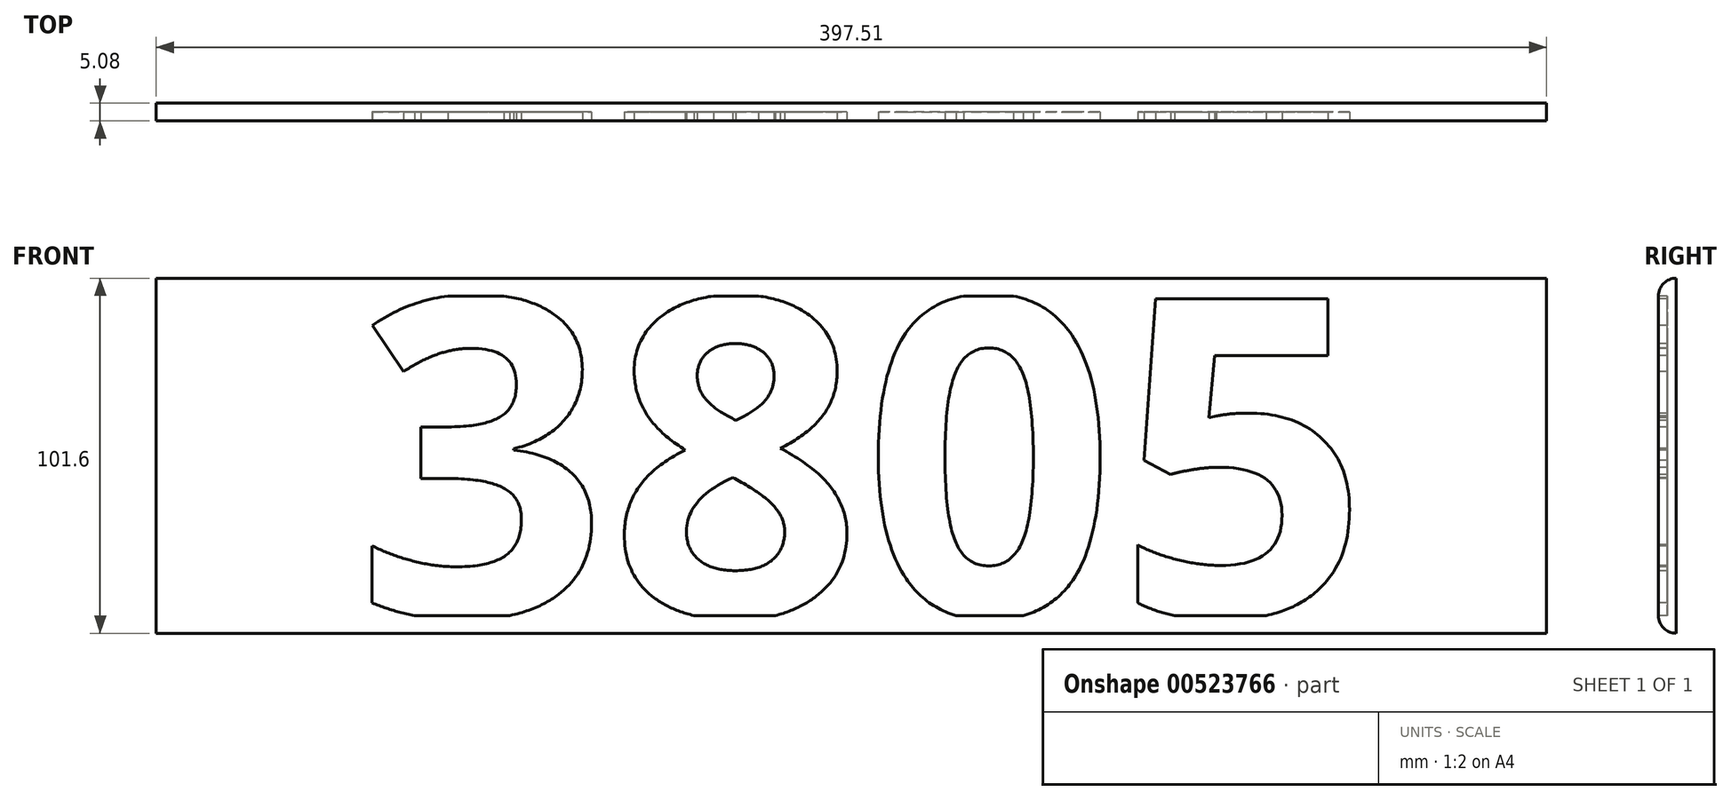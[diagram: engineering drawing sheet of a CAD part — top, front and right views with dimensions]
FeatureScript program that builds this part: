
annotation { "Feature Type Name" : "Feature", "Feature Type Description" : "" }
export const myFeature = defineFeature(function(context is Context, id is Id, definition is map)
    precondition{}
    {
        {
            var Q0;
            Q0=qCreatedBy(makeId("Right.planeOp"),FACE);
            var sketch = newSketch(context, id + "F0", { "sketchPlane" : qUnion([Q0])});
            skLineSegment(sketch, "E0", {"start": v(0, 0) * mm, "end": v(0, 101.6) * mm});
            skLineSegment(sketch, "E1", {"start": v(0, 101.6) * mm, "end": v(0, 101.6) * mm});
            skLineSegment(sketch, "E2", {"start": v(-5.08, 96.52) * mm, "end": v(-5.08, 5.08) * mm});
            skLineSegment(sketch, "E3", {"start": v(0, 0) * mm, "end": v(0, 0) * mm});
            skPoint(sketch, "E4.visualSharp", {"position": v(-5.08, 101.6) * mm});
            skArc(sketch, "E4.filletArc", {"start": v(0, 101.6) * mm, "mid": v(-3.6, 100.11) * mm, "end": v(-5.08, 96.52) * mm});
            skPoint(sketch, "E5.visualSharp", {"position": v(-5.08, 0) * mm});
            skArc(sketch, "E5.filletArc", {"start": v(-5.08, 5.08) * mm, "mid": v(-3.6, 1.49) * mm, "end": v(0, 0) * mm});
            skSolve(sketch);
        }
        {
            var Q0;
            Q0=makeQuery(id+"F0.imprint","IMPRINT",FACE,{"disambiguationData":[TD([[makeQuery(id+"F0.imprint","IMPRINT",EDGE,{"derivedFrom":sQuery(id+"F0.wireOp",EDGE,"E0")}),1.0]])]});
            extrude(context, id + "F1", {"entities" : qUnion([Q0]), "depth" : 397.5 * mm, "offsetDistance" : 25.4 * mm});
        }
        {
            var Q0;
            Q0=makeQuery(id+"F1.opExtrude","SWEPT_FACE",FACE,{"disambiguationData":[OSD([sQuery(id+"F0.wireOp",EDGE,"E2")])]});
            var sketch = newSketch(context, id + "F2", { "sketchPlane" : qUnion([Q0])});
            skText(sketch, "E6", { "text": "3805", "fontName": "OpenSans-Bold.ttf"});
            const initialGuessF2  = {"E6": [0.0569, 0.00508, 1, 0, 0.09144]};
            skSetInitialGuess(sketch, initialGuessF2);
            skSolve(sketch);
        }
        {
            var Q0;
            Q0=makeQuery(id+"F2.imprint","IMPRINT",FACE,{"disambiguationData":[TD([[makeQuery(id+"F2.imprint","IMPRINT",EDGE,{"derivedFrom":sQuery(id+"F2.wireOp",EDGE,"E6.sketch_text.stroke-0")}),-1.0]])]});
            var Q1;
            {var subQ5=sQuery(id+"F2.wireOp",EDGE,"E6.sketch_text.stroke-28");Q1=makeQuery(id+"F2.imprint","IMPRINT",FACE,{"disambiguationData":[TD([[makeQuery(id+"F2.imprint","IMPRINT",EDGE,{"derivedFrom":subQ5}),-1.0]])]});}
            var Q2;
            {var subQ8=sQuery(id+"F2.wireOp",EDGE,"E6.sketch_text.stroke-58");Q2=makeQuery(id+"F2.imprint","IMPRINT",FACE,{"disambiguationData":[TD([[makeQuery(id+"F2.imprint","IMPRINT",EDGE,{"derivedFrom":subQ8}),-1.0]])]});}
            var Q3;
            Q3=makeQuery(id+"F2.imprint","IMPRINT",FACE,{"disambiguationData":[TD([[makeQuery(id+"F2.imprint","IMPRINT",EDGE,{"derivedFrom":sQuery(id+"F2.wireOp",EDGE,"E6.sketch_text.stroke-74")}),-1.0]])]});
            extrude(context, id + "F3", {"entities" : qUnion([Q0, Q1, Q2, Q3]), "operationType" : NewBodyOperationType.REMOVE, "oppositeDirection" : true, "depth" : 2.54 * mm, "offsetDistance" : 25.4 * mm});
        }
    });
